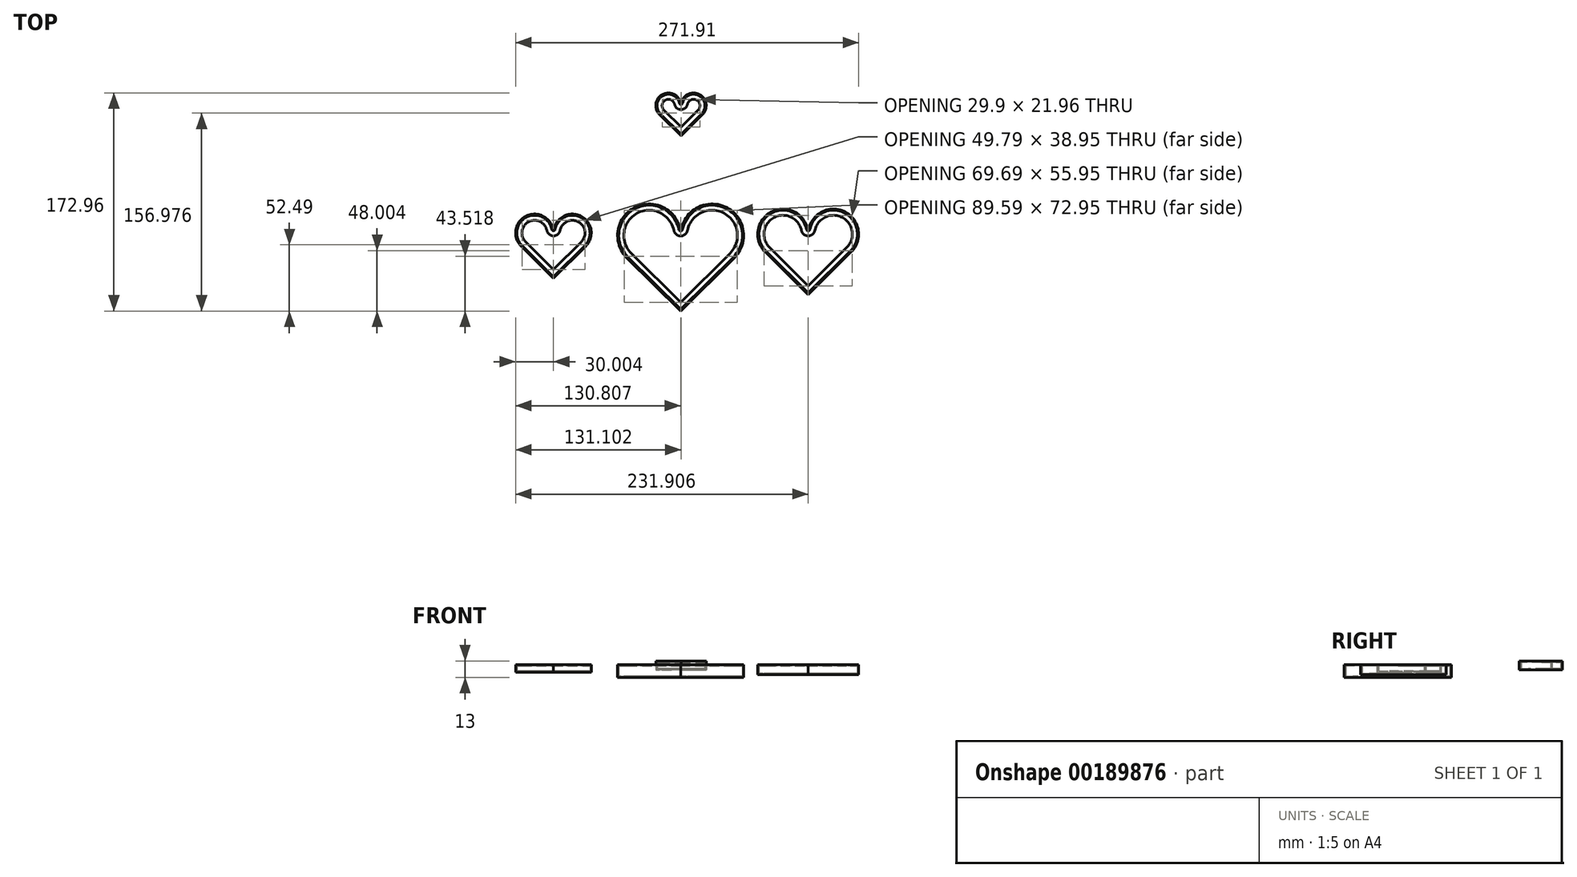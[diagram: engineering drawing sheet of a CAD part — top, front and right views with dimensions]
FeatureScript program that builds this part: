
annotation { "Feature Type Name" : "Feature", "Feature Type Description" : "" }
export const myFeature = defineFeature(function(context is Context, id is Id, definition is map)
    precondition{}
    {
        {
            var Q0;
            Q0=qCreatedBy(makeId("Top.planeOp"),FACE);
            var sketch = newSketch(context, id + "F0", { "sketchPlane" : qUnion([Q0])});
            skArc(sketch, "E0", {"start": v(-20.02, 27.7) * mm, "mid": v(-56.39, 44.78) * mm, "end": v(-62.14, 5.02) * mm});
            skLineSegment(sketch, "E1", {"start": v(-44.53, 22.77) * mm, "end": v(5.47, 22.77) * mm});
            skArc(sketch, "E2", {"start": v(23.07, 5.02) * mm, "mid": v(17.32, 44.78) * mm, "end": v(-19.04, 27.7) * mm});
            skLineSegment(sketch, "E3", {"start": v(-19.53, -37.23) * mm, "end": v(23.07, 5.02) * mm});
            skLineSegment(sketch, "E4", {"start": v(-19.53, -37.23) * mm, "end": v(-62.14, 5.02) * mm});
            skPoint(sketch, "E5.visualSharp", {"position": v(-19.53, 22.77) * mm});
            skArc(sketch, "E5.filletArc", {"start": v(-20.02, 27.7) * mm, "mid": v(-19.53, 27.3) * mm, "end": v(-19.04, 27.7) * mm});
            skSolve(sketch);
        }
        {
            var Q0;
            Q0 = qSketchRegion(id + "F0", true);
            extrude(context, id + "F1", {"entities" : qUnion([Q0]), "depth" : 10 * mm});
        }
        {
            var Q0;
            Q0=makeQuery(id+"F1.opExtrude","SWEPT_BODY",BODY,{"disambiguationData":[OSD([sQuery(id+"F0.wireOp",EDGE,"E0"),sQuery(id+"F0.wireOp",EDGE,"E2"),sQuery(id+"F0.wireOp",EDGE,"E3"),sQuery(id+"F0.wireOp",EDGE,"E4"),sQuery(id+"F0.wireOp",EDGE,"E5.filletArc")])]});
            transform(context, id + "F2", {"entities" : qUnion([Q0]), "transformType" : TransformType.TRANSLATION_3D, "dx" : 101 * mm, "dy" : 0 * mm, "dz" : 0 * mm, "makeCopy" : true});
        }
        {
            var Q0;
            Q0=makeQuery(id+"F2.opPattern","COPY",BODY,{"derivedFrom":makeQuery(id+"F1.opExtrude","SWEPT_BODY",BODY,{"disambiguationData":[OSD([sQuery(id+"F0.wireOp",EDGE,"E0"),sQuery(id+"F0.wireOp",EDGE,"E2"),sQuery(id+"F0.wireOp",EDGE,"E3"),sQuery(id+"F0.wireOp",EDGE,"E4"),sQuery(id+"F0.wireOp",EDGE,"E5.filletArc")])]}),"instanceName":"1"});
            var Q1;
            Q1=makeQuery(id+"F2.opPattern","COPY",VERTEX,{"derivedFrom":makeQuery(id+"F1.opExtrude","CAP_VERTEX",VERTEX,{"disambiguationData":[OSD([sQuery(id+"F0.wireOp",EDGE,"E2"),sQuery(id+"F0.wireOp",EDGE,"E5.filletArc")])],"isStart":false}),"instanceName":"1"});
            transform(context, id + "F3", {"entities" : qUnion([Q0]), "transformType" : TransformType.SCALE_UNIFORMLY, "scale" : .8, "scalePoint" : qUnion([Q1]), "makeCopy" : false});
        }
        {
            var Q0;
            Q0=makeQuery(id+"F1.opExtrude","SWEPT_BODY",BODY,{"disambiguationData":[OSD([sQuery(id+"F0.wireOp",EDGE,"E0"),sQuery(id+"F0.wireOp",EDGE,"E2"),sQuery(id+"F0.wireOp",EDGE,"E3"),sQuery(id+"F0.wireOp",EDGE,"E4"),sQuery(id+"F0.wireOp",EDGE,"E5.filletArc")])]});
            transform(context, id + "F4", {"entities" : qUnion([Q0]), "transformType" : TransformType.TRANSLATION_3D, "dx" : -101 * mm, "dy" : 0 * mm, "dz" : 0 * mm, "makeCopy" : true});
        }
        {
            var Q0;
            Q0=makeQuery(id+"F4.opPattern","COPY",BODY,{"derivedFrom":makeQuery(id+"F1.opExtrude","SWEPT_BODY",BODY,{"disambiguationData":[OSD([sQuery(id+"F0.wireOp",EDGE,"E0"),sQuery(id+"F0.wireOp",EDGE,"E2"),sQuery(id+"F0.wireOp",EDGE,"E3"),sQuery(id+"F0.wireOp",EDGE,"E4"),sQuery(id+"F0.wireOp",EDGE,"E5.filletArc")])]}),"instanceName":"1"});
            var Q1;
            Q1=makeQuery(id+"F4.opPattern","COPY",VERTEX,{"derivedFrom":makeQuery(id+"F1.opExtrude","CAP_VERTEX",VERTEX,{"disambiguationData":[OSD([sQuery(id+"F0.wireOp",EDGE,"E2"),sQuery(id+"F0.wireOp",EDGE,"E5.filletArc")])],"isStart":false}),"instanceName":"1"});
            transform(context, id + "F5", {"entities" : qUnion([Q0]), "transformType" : TransformType.SCALE_UNIFORMLY, "scale" : .6, "scalePoint" : qUnion([Q1]), "makeCopy" : false});
        }
        {
            var Q0;
            Q0=makeQuery(id+"F1.opExtrude","SWEPT_BODY",BODY,{"disambiguationData":[OSD([sQuery(id+"F0.wireOp",EDGE,"E0"),sQuery(id+"F0.wireOp",EDGE,"E2"),sQuery(id+"F0.wireOp",EDGE,"E3"),sQuery(id+"F0.wireOp",EDGE,"E4"),sQuery(id+"F0.wireOp",EDGE,"E5.filletArc")])]});
            transform(context, id + "F6", {"entities" : qUnion([Q0]), "transformType" : TransformType.TRANSLATION_3D, "dx" : 0 * mm, "dy" : 100 * mm, "dz" : 0 * mm, "makeCopy" : true});
        }
        {
            var Q0;
            Q0=makeQuery(id+"F6.opPattern","COPY",BODY,{"derivedFrom":makeQuery(id+"F1.opExtrude","SWEPT_BODY",BODY,{"disambiguationData":[OSD([sQuery(id+"F0.wireOp",EDGE,"E0"),sQuery(id+"F0.wireOp",EDGE,"E2"),sQuery(id+"F0.wireOp",EDGE,"E3"),sQuery(id+"F0.wireOp",EDGE,"E4"),sQuery(id+"F0.wireOp",EDGE,"E5.filletArc")])]}),"instanceName":"1"});
            var Q1;
            Q1=makeQuery(id+"F6.opPattern","COPY",VERTEX,{"derivedFrom":makeQuery(id+"F1.opExtrude","CAP_VERTEX",VERTEX,{"disambiguationData":[OSD([sQuery(id+"F0.wireOp",EDGE,"E2"),sQuery(id+"F0.wireOp",EDGE,"E5.filletArc")])],"isStart":false}),"instanceName":"1"});
            transform(context, id + "F7", {"entities" : qUnion([Q0]), "transformType" : TransformType.SCALE_UNIFORMLY, "scale" : .4, "scalePoint" : qUnion([Q1]), "makeCopy" : false});
        }
        {
            var Q0;
            Q0=makeQuery(id+"F1.opExtrude","CAP_FACE",FACE,{"disambiguationData":[OSD([sQuery(id+"F0.wireOp",EDGE,"E0"),sQuery(id+"F0.wireOp",EDGE,"E2"),sQuery(id+"F0.wireOp",EDGE,"E3"),sQuery(id+"F0.wireOp",EDGE,"E4"),sQuery(id+"F0.wireOp",EDGE,"E5.filletArc")])],"isStart":false});
            var Q1;
            Q1=makeQuery(id+"F2.opPattern","COPY",FACE,{"derivedFrom":makeQuery(id+"F1.opExtrude","CAP_FACE",FACE,{"disambiguationData":[OSD([sQuery(id+"F0.wireOp",EDGE,"E0"),sQuery(id+"F0.wireOp",EDGE,"E2"),sQuery(id+"F0.wireOp",EDGE,"E3"),sQuery(id+"F0.wireOp",EDGE,"E4"),sQuery(id+"F0.wireOp",EDGE,"E5.filletArc")])],"isStart":false}),"instanceName":"1"});
            var Q2;
            Q2=makeQuery(id+"F4.opPattern","COPY",FACE,{"derivedFrom":makeQuery(id+"F1.opExtrude","CAP_FACE",FACE,{"disambiguationData":[OSD([sQuery(id+"F0.wireOp",EDGE,"E0"),sQuery(id+"F0.wireOp",EDGE,"E2"),sQuery(id+"F0.wireOp",EDGE,"E3"),sQuery(id+"F0.wireOp",EDGE,"E4"),sQuery(id+"F0.wireOp",EDGE,"E5.filletArc")])],"isStart":false}),"instanceName":"1"});
            var Q3;
            Q3=makeQuery(id+"F6.opPattern","COPY",FACE,{"derivedFrom":makeQuery(id+"F1.opExtrude","CAP_FACE",FACE,{"disambiguationData":[OSD([sQuery(id+"F0.wireOp",EDGE,"E0"),sQuery(id+"F0.wireOp",EDGE,"E2"),sQuery(id+"F0.wireOp",EDGE,"E3"),sQuery(id+"F0.wireOp",EDGE,"E4"),sQuery(id+"F0.wireOp",EDGE,"E5.filletArc")])],"isStart":false}),"instanceName":"1"});
            shell(context, id + "F8", {"entities" : qUnion([Q0, Q1, Q2, Q3]), "thickness" : 1 * mm});
        }
        {
            var Q0;
            Q0=makeQuery(id+"F1.opExtrude","CAP_FACE",FACE,{"disambiguationData":[OSD([sQuery(id+"F0.wireOp",EDGE,"E0"),sQuery(id+"F0.wireOp",EDGE,"E2"),sQuery(id+"F0.wireOp",EDGE,"E3"),sQuery(id+"F0.wireOp",EDGE,"E4"),sQuery(id+"F0.wireOp",EDGE,"E5.filletArc")])],"isStart":true});
            var sketch = newSketch(context, id + "F9", { "sketchPlane" : qUnion([Q0])});
            skArc(sketch, "E6.0", {"start": v(-20.02, -27.7) * mm, "mid": v(-56.39, -44.78) * mm, "end": v(-62.14, -5.02) * mm});
            skLineSegment(sketch, "E7.0", {"start": v(-19.53, 30.19) * mm, "end": v(-58.62, -8.57) * mm});
            skArc(sketch, "E7.1", {"start": v(-24.92, -26.71) * mm, "mid": v(-54.02, -40.38) * mm, "end": v(-58.62, -8.57) * mm});
            skLineSegment(sketch, "E7.2", {"start": v(-19.53, 30.19) * mm, "end": v(19.55, -8.57) * mm});
            skArc(sketch, "E7.3", {"start": v(19.55, -8.57) * mm, "mid": v(14.95, -40.38) * mm, "end": v(-14.14, -26.71) * mm});
            skArc(sketch, "E7.4", {"start": v(-24.92, -26.71) * mm, "mid": v(-19.53, -22.3) * mm, "end": v(-14.14, -26.71) * mm});
            skSolve(sketch);
        }
        {
            var Q0;
            Q0 = qSketchRegion(id + "F9", true);
            extrude(context, id + "F10", {"entities" : qUnion([Q0]), "operationType" : NewBodyOperationType.REMOVE, "oppositeDirection" : true, "depth" : 25 * mm});
        }
        {
            var Q0;
            Q0=makeQuery(id+"F2.opPattern","COPY",FACE,{"derivedFrom":makeQuery(id+"F1.opExtrude","CAP_FACE",FACE,{"disambiguationData":[OSD([sQuery(id+"F0.wireOp",EDGE,"E0"),sQuery(id+"F0.wireOp",EDGE,"E2"),sQuery(id+"F0.wireOp",EDGE,"E3"),sQuery(id+"F0.wireOp",EDGE,"E4"),sQuery(id+"F0.wireOp",EDGE,"E5.filletArc")])],"isStart":true}),"instanceName":"1"});
            var sketch = newSketch(context, id + "F11", { "sketchPlane" : qUnion([Q0])});
            skArc(sketch, "E8.0", {"start": v(76.27, -26.71) * mm, "mid": v(81.57, -22.38) * mm, "end": v(86.86, -26.71) * mm});
            skArc(sketch, "E8.1", {"start": v(112.13, -13.1) * mm, "mid": v(108.68, -36.96) * mm, "end": v(86.86, -26.71) * mm});
            skArc(sketch, "E8.2", {"start": v(76.27, -26.71) * mm, "mid": v(54.45, -36.96) * mm, "end": v(51, -13.1) * mm});
            skLineSegment(sketch, "E8.3", {"start": v(81.57, 17.2) * mm, "end": v(51, -13.1) * mm});
            skLineSegment(sketch, "E8.4", {"start": v(81.57, 17.2) * mm, "end": v(112.13, -13.1) * mm});
            skSolve(sketch);
        }
        {
            var Q0;
            Q0 = qSketchRegion(id + "F11", true);
            extrude(context, id + "F12", {"entities" : qUnion([Q0]), "operationType" : NewBodyOperationType.REMOVE, "oppositeDirection" : true, "depth" : 25 * mm});
        }
        {
            var Q0;
            Q0=makeQuery(id+"F4.opPattern","COPY",FACE,{"derivedFrom":makeQuery(id+"F1.opExtrude","CAP_FACE",FACE,{"disambiguationData":[OSD([sQuery(id+"F0.wireOp",EDGE,"E0"),sQuery(id+"F0.wireOp",EDGE,"E2"),sQuery(id+"F0.wireOp",EDGE,"E3"),sQuery(id+"F0.wireOp",EDGE,"E4"),sQuery(id+"F0.wireOp",EDGE,"E5.filletArc")])],"isStart":true}),"instanceName":"1"});
            var sketch = newSketch(context, id + "F13", { "sketchPlane" : qUnion([Q0])});
            skLineSegment(sketch, "E9.0", {"start": v(-120.34, 4.22) * mm, "end": v(-142.38, -17.64) * mm});
            skArc(sketch, "E9.1", {"start": v(-125.53, -26.71) * mm, "mid": v(-140.08, -33.55) * mm, "end": v(-142.38, -17.64) * mm});
            skLineSegment(sketch, "E9.2", {"start": v(-120.34, 4.22) * mm, "end": v(-98.3, -17.64) * mm});
            skArc(sketch, "E9.3", {"start": v(-98.3, -17.64) * mm, "mid": v(-100.6, -33.55) * mm, "end": v(-115.14, -26.71) * mm});
            skArc(sketch, "E9.4", {"start": v(-125.53, -26.71) * mm, "mid": v(-120.34, -22.46) * mm, "end": v(-115.14, -26.71) * mm});
            skSolve(sketch);
        }
        {
            var Q0;
            Q0=makeQuery(id+"F13.imprint","IMPRINT",FACE,{"disambiguationData":[TD([[makeQuery(id+"F13.imprint","IMPRINT",EDGE,{"derivedFrom":sQuery(id+"F13.wireOp",EDGE,"E9.0")}),1.0]])]});
            extrude(context, id + "F14", {"entities" : qUnion([Q0]), "operationType" : NewBodyOperationType.REMOVE, "oppositeDirection" : true, "depth" : 25 * mm});
        }
        {
            var Q0;
            Q0=makeQuery(id+"F6.opPattern","COPY",FACE,{"derivedFrom":makeQuery(id+"F1.opExtrude","CAP_FACE",FACE,{"disambiguationData":[OSD([sQuery(id+"F0.wireOp",EDGE,"E0"),sQuery(id+"F0.wireOp",EDGE,"E2"),sQuery(id+"F0.wireOp",EDGE,"E3"),sQuery(id+"F0.wireOp",EDGE,"E4"),sQuery(id+"F0.wireOp",EDGE,"E5.filletArc")])],"isStart":true}),"instanceName":"1"});
            var sketch = newSketch(context, id + "F15", { "sketchPlane" : qUnion([Q0])});
            skArc(sketch, "E10.0", {"start": v(-24.34, -126.71) * mm, "mid": v(-19.24, -122.54) * mm, "end": v(-14.14, -126.71) * mm});
            skArc(sketch, "E10.1", {"start": v(-5.72, -122.18) * mm, "mid": v(-6.87, -130.13) * mm, "end": v(-14.14, -126.71) * mm});
            skArc(sketch, "E10.2", {"start": v(-24.34, -126.71) * mm, "mid": v(-31.6, -130.13) * mm, "end": v(-32.76, -122.18) * mm});
            skLineSegment(sketch, "E10.3", {"start": v(-19.24, -108.77) * mm, "end": v(-32.76, -122.18) * mm});
            skLineSegment(sketch, "E10.4", {"start": v(-19.24, -108.77) * mm, "end": v(-5.72, -122.18) * mm});
            skSolve(sketch);
        }
        {
            var Q0;
            Q0 = qSketchRegion(id + "F15", true);
            extrude(context, id + "F16", {"entities" : qUnion([Q0]), "operationType" : NewBodyOperationType.REMOVE, "oppositeDirection" : true, "depth" : 25 * mm});
        }
        {
            var Q0;
            {var subQ0=sQuery(id+"F0.wireOp",EDGE,"E2");Q0=makeQuery(id+"F8.opShell","OFFSET_EDGE",EDGE,{"disambiguationData":[OSD([subQ0]),TDD([makeQuery(id+"F1.opExtrude","CAP_EDGE",EDGE,{"disambiguationData":[OSD([subQ0])],"isStart":false})])]});}
            var Q1;
            {var subQ0=sQuery(id+"F0.wireOp",EDGE,"E5.filletArc");Q1=makeQuery(id+"F8.opShell","OFFSET_EDGE",EDGE,{"disambiguationData":[OSD([subQ0]),TDD([makeQuery(id+"F1.opExtrude","CAP_EDGE",EDGE,{"disambiguationData":[OSD([subQ0])],"isStart":false})])]});}
            chamfer(context, id + "F17", {"entities" : qUnion([Q0, Q1]), "width" : 1 * mm, "tangentPropagation" : true});
        }
        {
            var Q0;
            {var subQ0=sQuery(id+"F0.wireOp",EDGE,"E0");Q0=makeQuery(id+"F8.opShell","OFFSET_EDGE",EDGE,{"disambiguationData":[OSD([subQ0]),TDD([makeQuery(id+"F2.opPattern","COPY",EDGE,{"derivedFrom":makeQuery(id+"F1.opExtrude","CAP_EDGE",EDGE,{"disambiguationData":[OSD([subQ0])],"isStart":false}),"instanceName":"1"})])]});}
            chamfer(context, id + "F18", {"entities" : qUnion([Q0]), "width" : 1 * mm, "tangentPropagation" : true});
        }
        {
            var Q0;
            {var subQ0=sQuery(id+"F0.wireOp",EDGE,"E2");Q0=makeQuery(id+"F8.opShell","OFFSET_EDGE",EDGE,{"disambiguationData":[OSD([subQ0]),TDD([makeQuery(id+"F4.opPattern","COPY",EDGE,{"derivedFrom":makeQuery(id+"F1.opExtrude","CAP_EDGE",EDGE,{"disambiguationData":[OSD([subQ0])],"isStart":false}),"instanceName":"1"})])]});}
            chamfer(context, id + "F19", {"entities" : qUnion([Q0]), "width" : 1 * mm, "tangentPropagation" : true});
        }
        {
            var Q0;
            Q0=makeQuery(id+"F6.opPattern","COPY",FACE,{"derivedFrom":makeQuery(id+"F1.opExtrude","CAP_FACE",FACE,{"disambiguationData":[OSD([sQuery(id+"F0.wireOp",EDGE,"E0"),sQuery(id+"F0.wireOp",EDGE,"E2"),sQuery(id+"F0.wireOp",EDGE,"E3"),sQuery(id+"F0.wireOp",EDGE,"E4"),sQuery(id+"F0.wireOp",EDGE,"E5.filletArc")])],"isStart":false}),"instanceName":"1"});
            extrude(context, id + "F20", {"entities" : qUnion([Q0]), "operationType" : NewBodyOperationType.ADD, "depth" : 3 * mm});
        }
        {
            var Q0;
            {var subQ0=sQuery(id+"F0.wireOp",EDGE,"E2");Q0=makeQuery(id+"F20.opExtrude","CAP_EDGE",EDGE,{"disambiguationData":[OSD([subQ0]),TDD([makeQuery(id+"F8.opShell","OFFSET_EDGE",EDGE,{"disambiguationData":[OSD([subQ0]),TDD([makeQuery(id+"F6.opPattern","COPY",EDGE,{"derivedFrom":makeQuery(id+"F1.opExtrude","CAP_EDGE",EDGE,{"disambiguationData":[OSD([subQ0])],"isStart":false}),"instanceName":"1"})])]})])],"isStart":false});}
            chamfer(context, id + "F21", {"entities" : qUnion([Q0]), "width" : 1 * mm, "tangentPropagation" : true});
        }
    });
